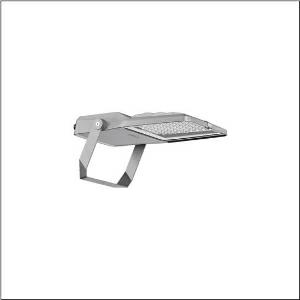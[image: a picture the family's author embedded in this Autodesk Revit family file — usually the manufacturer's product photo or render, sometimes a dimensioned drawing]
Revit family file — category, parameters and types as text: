
# Revit family: floodlight_fl_21_mini___pl33t_5xa7772c4f1a_51a0
name_source: partatom
category: Lighting Fixtures
units: mm (PartAtom-declared; Revit-internal decimal feet)

## family parameters
Cut with Voids When Loaded = No
Host = Face
Light Source = No
Part Type = Normal
Room Calculation Point = No
Round Connector Dimension = Use Diameter
Shared = No

## types (1)
- --- (1 x LED, 12570 lm, 87.2 W, 4000K)
    Apparent Load = 87 VA
    CIE Flux Codes = 26 75 99 100 100
    Color Rendering = 70
    Color Temperature = 4000K
    Default Elevation = 1800 mm
    Description = Floodlight FL 21 mini, floodlight, primary light control with lens, of PMMA, primary optical cover: protective disc, of toughened safety glass, transparent, light distribution: PL33T, light emission: direct distribution, installation type: surface-mounted, LED, High Power LED, rated luminous flux: 12.570lm, luminous efficacy: 144lm/W, light colour: 740, colour temperature: 4000K, control gear: ECG iQ, control: Street-Remote, Auto-Match, Temp-Guard, Night-Set, Smart-Wire, Desk-Remote (wireless, voltage-free reading and setting of iQ features in the workshop via application-optimized NFC function/RFID function), optimised constant luminous flux control (CLO 2.0), with terminal, 6-pole, mains connection: 220..240V, AC, 50/60Hz, start of lifetime: 87W, end of lifetime: 92W, reduction: 40W, luminaire housing, of diecast aluminium, powder-coated, Siteco® metallic grey (DB 702S), corrosivity category C5 according to DIN EN ISO 12944, mounting bracket, of steel, galvanised, powder-coated, Siteco® metallic grey (DB 702S), protection rating (complete): IP66, insulation class (complete): insulation class II (safety insulation), certification: CE, ENEC, VDE, protection symbol: D, impact resistance: IK08, permissible operating ambient temperature: -40..+40°C, permissible operating ambient temperature for outdoor applications: -40..+50°C, standard: DIN EN 12944, packaging unit: 1 piece

Light Distribution: PL33T
    Height = 70 mm
    Lamp = 1 x LED
    Lamp Light Flux = 12570 lm
    Lamp Power = 87.2 W
    Lamp count = 1
    Length = 485 mm
    Luminous efficacy = 144 lm/W
    Manufacturer = Siteco
    ModVariant = No
    Model = 5XA7772C4F1A
    Number of Poles = 1
    OnlyDefault = Yes
    Power Factor = 1
    Product Name = Floodlight FL 21 mini | PL33T
    Product group = floodlight | pylon top
    ProductGroupID = 6101
    Protection Class = Protection class II
    Protection Degree = IP 66
    RLX_Detail_Level = 1
    RlxData = <blob elided: 96077 chars, md5=8847d37a>
    Socket = socket
    Standby Power = 0 W
    System Light Flux = 12570 lm
    System Power = 87 W
    Type Comments = factory setting: luminous flux: 100 % | dim-lin: 254 | 456 mA
    Type Image = l_1006845.jpg
    URL = http://relux.com
    VarID = @adj_059441
    Voltage = 0 V
    Weight = 0.00 kg
    Width = 337 mm

## geometry (parser evidence)
native form markers: Blend x4, Sweep x15
no freeform markers — native parametric forms only
